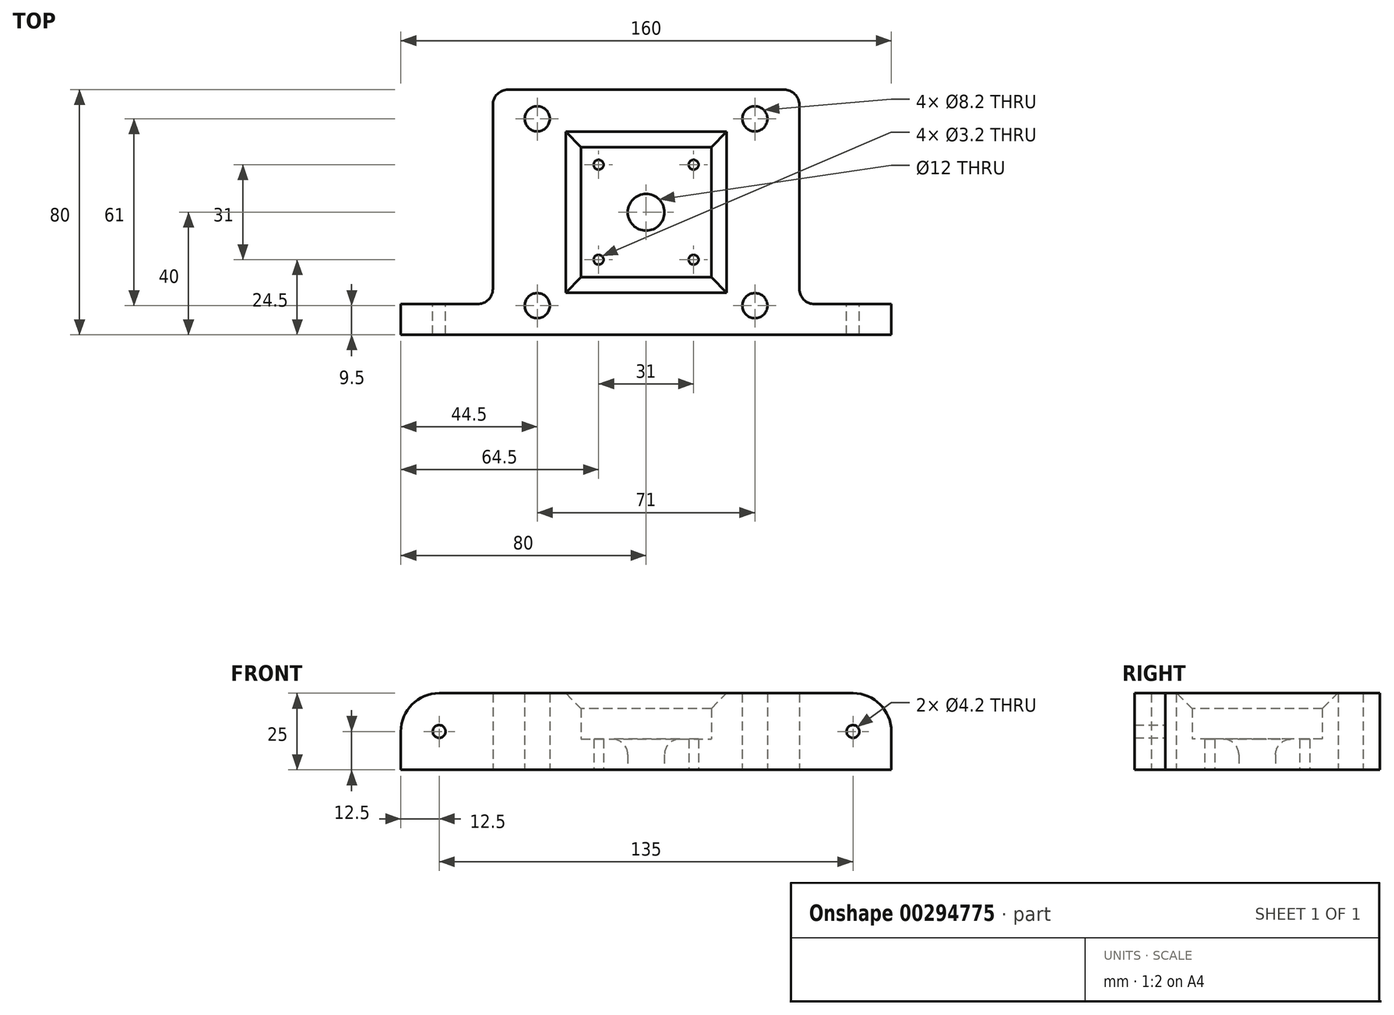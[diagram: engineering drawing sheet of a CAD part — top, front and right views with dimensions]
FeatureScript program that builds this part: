
annotation { "Feature Type Name" : "Feature", "Feature Type Description" : "" }
export const myFeature = defineFeature(function(context is Context, id is Id, definition is map)
    precondition{}
    {
        {
            var Q0;
            Q0=qCreatedBy(makeId("Top.planeOp"),FACE);
            var sketch = newSketch(context, id + "F0", { "sketchPlane" : qUnion([Q0])});
            skLineSegment(sketch, "E0.top", {"start": v(-50, -40) * mm, "end": v(50, -40) * mm});
            skPoint(sketch, "E0.middle", {"position": v(0, 0) * mm});
            skLineSegment(sketch, "E1.bottom", {"start": v(-15.5, 15.5) * mm, "end": v(15.5, 15.5) * mm, "construction": true});
            skLineSegment(sketch, "E1.top", {"start": v(-15.5, -15.5) * mm, "end": v(15.5, -15.5) * mm, "construction": true});
            skLineSegment(sketch, "E1.left", {"start": v(-15.5, 15.5) * mm, "end": v(-15.5, -15.5) * mm, "construction": true});
            skLineSegment(sketch, "E1.right", {"start": v(15.5, 15.5) * mm, "end": v(15.5, -15.5) * mm, "construction": true});
            skCircle(sketch, "E2", {"center": v(-15.5, 15.5) * mm, "radius": 1.6 * mm});
            skCircle(sketch, "E3", {"center": v(15.5, 15.5) * mm, "radius": 1.6 * mm});
            skCircle(sketch, "E4", {"center": v(15.5, -15.5) * mm, "radius": 1.6 * mm});
            skCircle(sketch, "E5", {"center": v(-15.5, -15.5) * mm, "radius": 1.6 * mm});
            skPoint(sketch, "E6.orphan", {"position": v(-50, 40) * mm});
            skPoint(sketch, "E7.orphan", {"position": v(50, 40) * mm});
            skPoint(sketch, "E0.left.start.orphan", {"position": v(-50, 21) * mm});
            skPoint(sketch, "E0.right.start.orphan", {"position": v(50, 21) * mm});
            skLineSegment(sketch, "E8", {"start": v(-50, 40) * mm, "end": v(-50, -40) * mm});
            skLineSegment(sketch, "E9", {"start": v(50, 40) * mm, "end": v(50, -40) * mm});
            skLineSegment(sketch, "E10", {"start": v(50, 40) * mm, "end": v(-50, 40) * mm});
            skLineSegment(sketch, "E11", {"start": v(50, 21) * mm, "end": v(21, 21) * mm, "construction": true});
            skLineSegment(sketch, "E12", {"start": v(-50, -40) * mm, "end": v(-21, -21) * mm, "construction": true});
            skLineSegment(sketch, "E13", {"start": v(-21, -21) * mm, "end": v(-50, -21) * mm, "construction": true});
            skLineSegment(sketch, "E14", {"start": v(-21, -21) * mm, "end": v(-21, -40) * mm, "construction": true});
            skLineSegment(sketch, "E15", {"start": v(-21, -40) * mm, "end": v(-50, -21) * mm, "construction": true});
            skLineSegment(sketch, "E16", {"start": v(-50, 21) * mm, "end": v(-21, 21) * mm, "construction": true});
            skLineSegment(sketch, "E17", {"start": v(21, -21) * mm, "end": v(21, -40) * mm, "construction": true});
            skLineSegment(sketch, "E18", {"start": v(21, -21) * mm, "end": v(50, -21) * mm, "construction": true});
            skLineSegment(sketch, "E19", {"start": v(50, -21) * mm, "end": v(21, -40) * mm, "construction": true});
            skLineSegment(sketch, "E20", {"start": v(50, -40) * mm, "end": v(21, -21) * mm, "construction": true});
            skCircle(sketch, "E21", {"center": v(-35.5, -30.5) * mm, "radius": 4.1 * mm});
            skCircle(sketch, "E22", {"center": v(35.5, -30.5) * mm, "radius": 4.1 * mm});
            skLineSegment(sketch, "E23", {"start": v(-21, 21) * mm, "end": v(-21, 40) * mm, "construction": true});
            skLineSegment(sketch, "E24", {"start": v(21, 21) * mm, "end": v(21, 40) * mm, "construction": true});
            skLineSegment(sketch, "E25", {"start": v(-21, 40) * mm, "end": v(-50, 21) * mm, "construction": true});
            skLineSegment(sketch, "E26", {"start": v(-50, 40) * mm, "end": v(-21, 21) * mm, "construction": true});
            skLineSegment(sketch, "E27", {"start": v(21, 40) * mm, "end": v(50, 21) * mm, "construction": true});
            skLineSegment(sketch, "E28", {"start": v(50, 40) * mm, "end": v(21, 21) * mm, "construction": true});
            skCircle(sketch, "E29", {"center": v(-35.5, 30.5) * mm, "radius": 4.1 * mm});
            skCircle(sketch, "E30", {"center": v(35.5, 30.5) * mm, "radius": 4.1 * mm});
            skLineSegment(sketch, "E31.bottom", {"start": v(-21.25, 21.25) * mm, "end": v(21.25, 21.25) * mm});
            skLineSegment(sketch, "E31.top", {"start": v(-21.25, -21.25) * mm, "end": v(21.25, -21.25) * mm});
            skLineSegment(sketch, "E31.left", {"start": v(-21.25, 21.25) * mm, "end": v(-21.25, -21.25) * mm});
            skLineSegment(sketch, "E31.right", {"start": v(21.25, 21.25) * mm, "end": v(21.25, -21.25) * mm});
            skCircle(sketch, "E32", {"center": v(0, 0) * mm, "radius": 6 * mm});
            skLineSegment(sketch, "E33.bottom", {"start": v(50, -40) * mm, "end": v(80, -40) * mm});
            skLineSegment(sketch, "E33.top", {"start": v(50, -30) * mm, "end": v(80, -30) * mm});
            skLineSegment(sketch, "E33.left", {"start": v(50, -40) * mm, "end": v(50, -30) * mm});
            skLineSegment(sketch, "E33.right", {"start": v(80, -40) * mm, "end": v(80, -30) * mm});
            skLineSegment(sketch, "E34.bottom", {"start": v(-50, -40) * mm, "end": v(-80, -40) * mm});
            skLineSegment(sketch, "E34.top", {"start": v(-50, -30) * mm, "end": v(-80, -30) * mm});
            skLineSegment(sketch, "E34.left", {"start": v(-50, -40) * mm, "end": v(-50, -30) * mm});
            skLineSegment(sketch, "E34.right", {"start": v(-80, -40) * mm, "end": v(-80, -30) * mm});
            skLineSegment(sketch, "E35", {"start": v(0, 0) * mm, "end": v(-35.5, 0) * mm, "construction": true});
            skLineSegment(sketch, "E36", {"start": v(-35.5, 30.5) * mm, "end": v(-35.5, 0) * mm, "construction": true});
            skSolve(sketch);
        }
        {
            var Q0;
            Q0=makeQuery(id+"F0.imprint","IMPRINT",FACE,{"disambiguationData":[TD([[makeQuery(id+"F0.imprint","IMPRINT",EDGE,{"derivedFrom":sQuery(id+"F0.wireOp",EDGE,"E0.top")}),1.0]])]});
            var Q1;
            Q1=makeQuery(id+"F0.imprint","IMPRINT",FACE,{"disambiguationData":[TD([[makeQuery(id+"F0.imprint","IMPRINT",EDGE,{"derivedFrom":sQuery(id+"F0.wireOp",EDGE,"E34.bottom")}),-1.0]])]});
            var Q2;
            Q2=makeQuery(id+"F0.imprint","IMPRINT",FACE,{"disambiguationData":[TD([[makeQuery(id+"F0.imprint","IMPRINT",EDGE,{"derivedFrom":sQuery(id+"F0.wireOp",EDGE,"E33.bottom")}),1.0]])]});
            extrude(context, id + "F1", {"entities" : qUnion([Q0, Q1, Q2]), "depth" : 25 * mm});
        }
        {
            var Q0;
            Q0=makeQuery(id+"F0.imprint","IMPRINT",FACE,{"disambiguationData":[TD([[makeQuery(id+"F0.imprint","IMPRINT",EDGE,{"derivedFrom":sQuery(id+"F0.wireOp",EDGE,"E2")}),-1.0]])]});
            extrude(context, id + "F2", {"entities" : qUnion([Q0]), "operationType" : NewBodyOperationType.ADD, "depth" : 10 * mm});
        }
        {
            var Q0;
            Q0=makeQuery(id+"F1.opExtrude","CAP_EDGE",EDGE,{"disambiguationData":[OSD([sQuery(id+"F0.wireOp",EDGE,"E31.left")])],"isStart":false});
            var Q1;
            Q1=makeQuery(id+"F1.opExtrude","CAP_EDGE",EDGE,{"disambiguationData":[OSD([sQuery(id+"F0.wireOp",EDGE,"E31.bottom")])],"isStart":false});
            var Q2;
            Q2=makeQuery(id+"F1.opExtrude","CAP_EDGE",EDGE,{"disambiguationData":[OSD([sQuery(id+"F0.wireOp",EDGE,"E31.right")])],"isStart":false});
            var Q3;
            Q3=makeQuery(id+"F1.opExtrude","CAP_EDGE",EDGE,{"disambiguationData":[OSD([sQuery(id+"F0.wireOp",EDGE,"E31.top")])],"isStart":false});
            chamfer(context, id + "F3", {"entities" : qUnion([Q0, Q1, Q2, Q3]), "width" : 5 * mm, "tangentPropagation" : true});
        }
        {
            var Q0;
            Q0=makeQuery(id+"F2.opExtrude","CAP_EDGE",EDGE,{"disambiguationData":[OSD([sQuery(id+"F0.wireOp",EDGE,"E32")])],"isStart":false});
            fillet(context, id + "F4", {"entities" : qUnion([Q0]), "radius" : 5 * mm, "tangentPropagation" : true, "allowEdgeOverflow" : false});
        }
        {
            var Q0;
            Q0=makeQuery(id+"F1.opExtrude","SWEPT_EDGE",EDGE,{"disambiguationData":[OSD([sQuery(id+"F0.wireOp",EDGE,"E9"),sQuery(id+"F0.wireOp",EDGE,"E33.top"),sQuery(id+"F0.wireOp",EDGE,"E33.left")])]});
            var Q1;
            Q1=makeQuery(id+"F1.opExtrude","SWEPT_EDGE",EDGE,{"disambiguationData":[OSD([sQuery(id+"F0.wireOp",EDGE,"E8"),sQuery(id+"F0.wireOp",EDGE,"E34.top"),sQuery(id+"F0.wireOp",EDGE,"E34.left")])]});
            var Q2;
            Q2=makeQuery(id+"F1.opExtrude","SWEPT_EDGE",EDGE,{"disambiguationData":[OSD([sQuery(id+"F0.wireOp",EDGE,"E8"),sQuery(id+"F0.wireOp",EDGE,"E10")])]});
            var Q3;
            Q3=makeQuery(id+"F1.opExtrude","SWEPT_EDGE",EDGE,{"disambiguationData":[OSD([sQuery(id+"F0.wireOp",EDGE,"E9"),sQuery(id+"F0.wireOp",EDGE,"E10")])]});
            fillet(context, id + "F5", {"entities" : qUnion([Q0, Q1, Q2, Q3]), "radius" : 5 * mm, "tangentPropagation" : true, "allowEdgeOverflow" : false});
        }
        {
            var Q0;
            Q0=makeQuery(id+"F1.opExtrude","SWEPT_FACE",FACE,{"disambiguationData":[OSD([sQuery(id+"F0.wireOp",EDGE,"E34.top")])]});
            var sketch = newSketch(context, id + "F6", { "sketchPlane" : qUnion([Q0])});
            skLineSegment(sketch, "E37", {"start": v(80, 25) * mm, "end": v(55, 0) * mm, "construction": true});
            skLineSegment(sketch, "E38", {"start": v(80, 0) * mm, "end": v(55, 25) * mm, "construction": true});
            skCircle(sketch, "E39", {"center": v(67.5, 12.5) * mm, "radius": 2.1 * mm});
            skSolve(sketch);
        }
        {
            var Q0;
            Q0=makeQuery(id+"F6.imprint","IMPRINT",FACE,{"disambiguationData":[TD([[makeQuery(id+"F6.imprint","IMPRINT",EDGE,{"derivedFrom":sQuery(id+"F6.wireOp",EDGE,"E39")}),1.0]])]});
            extrude(context, id + "F7", {"entities" : qUnion([Q0]), "operationType" : NewBodyOperationType.REMOVE, "oppositeDirection" : true, "depth" : 25 * mm});
        }
        {
            var Q0;
            Q0=makeQuery(id+"F1.opExtrude","CAP_EDGE",EDGE,{"disambiguationData":[OSD([sQuery(id+"F0.wireOp",EDGE,"E34.right")])],"isStart":false});
            var Q1;
            Q1=makeQuery(id+"F1.opExtrude","CAP_EDGE",EDGE,{"disambiguationData":[OSD([sQuery(id+"F0.wireOp",EDGE,"E33.right")])],"isStart":false});
            fillet(context, id + "F8", {"entities" : qUnion([Q0, Q1]), "radius" : 12.5 * mm, "tangentPropagation" : true, "allowEdgeOverflow" : false});
        }
        {
            var Q0;
            Q0=makeQuery(id+"F1.opExtrude","SWEPT_FACE",FACE,{"disambiguationData":[OSD([sQuery(id+"F0.wireOp",EDGE,"E33.top")])]});
            var sketch = newSketch(context, id + "F9", { "sketchPlane" : qUnion([Q0])});
            skCircle(sketch, "E40", {"center": v(-67.5, 12.5) * mm, "radius": 2.1 * mm});
            skSolve(sketch);
        }
        {
            var Q0;
            Q0=makeQuery(id+"F9.imprint","IMPRINT",FACE,{"disambiguationData":[TD([[makeQuery(id+"F9.imprint","IMPRINT",EDGE,{"derivedFrom":sQuery(id+"F9.wireOp",EDGE,"E40")}),1.0]])]});
            extrude(context, id + "F10", {"entities" : qUnion([Q0]), "operationType" : NewBodyOperationType.REMOVE, "oppositeDirection" : true, "depth" : 25 * mm});
        }
    });
